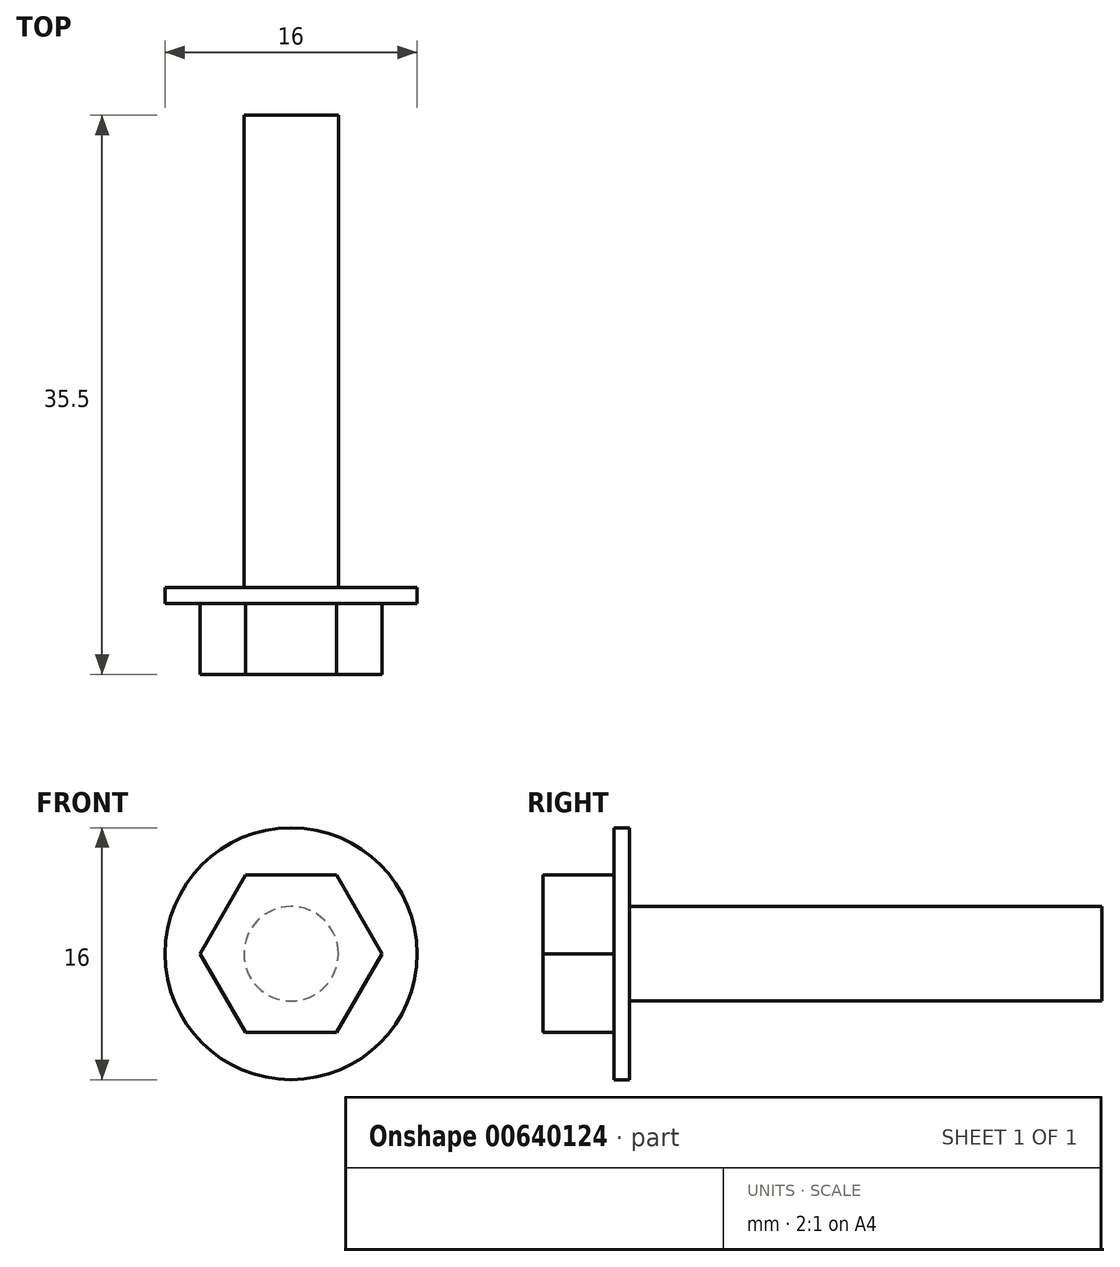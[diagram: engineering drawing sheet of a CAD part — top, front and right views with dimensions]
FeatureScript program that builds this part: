
annotation { "Feature Type Name" : "Feature", "Feature Type Description" : "" }
export const myFeature = defineFeature(function(context is Context, id is Id, definition is map)
    precondition{}
    {
        {
            var Q0;
            Q0=qCreatedBy(makeId("Front.planeOp"),FACE);
            var sketch = newSketch(context, id + "F0", { "sketchPlane" : qUnion([Q0])});
            skLineSegment(sketch, "E0", {"start": v(2.89, 0) * mm, "end": v(8.66, 0) * mm});
            skLineSegment(sketch, "E1", {"start": v(8.66, 0) * mm, "end": v(11.55, 5) * mm});
            skLineSegment(sketch, "E2", {"start": v(11.55, 5) * mm, "end": v(8.66, 10) * mm});
            skLineSegment(sketch, "E3", {"start": v(8.66, 10) * mm, "end": v(2.89, 10) * mm});
            skLineSegment(sketch, "E4", {"start": v(2.89, 10) * mm, "end": v(0, 5) * mm});
            skLineSegment(sketch, "E5", {"start": v(0, 5) * mm, "end": v(2.89, 0) * mm});
            skLineSegment(sketch, "E6", {"start": v(2.89, 10) * mm, "end": v(8.66, 0) * mm, "construction": true});
            skLineSegment(sketch, "E7", {"start": v(2.89, 0) * mm, "end": v(8.66, 10) * mm, "construction": true});
            skLineSegment(sketch, "E8", {"start": v(0, 5) * mm, "end": v(11.55, 5) * mm, "construction": true});
            skSolve(sketch);
        }
        {
            var Q0;
            Q0 = qSketchRegion(id + "F0", true);
            extrude(context, id + "F1", {"entities" : qUnion([Q0]), "depth" : 5.5 * mm, "offsetDistance" : 25 * mm});
        }
        {
            var Q0;
            Q0=makeQuery(id+"F1.opExtrude","CAP_FACE",FACE,{"disambiguationData":[OSD([sQuery(id+"F0.wireOp",EDGE,"E0"),sQuery(id+"F0.wireOp",EDGE,"E1"),sQuery(id+"F0.wireOp",EDGE,"E2"),sQuery(id+"F0.wireOp",EDGE,"E3"),sQuery(id+"F0.wireOp",EDGE,"E4"),sQuery(id+"F0.wireOp",EDGE,"E5")])],"isStart":true});
            var sketch = newSketch(context, id + "F2", { "sketchPlane" : qUnion([Q0])});
            skCircle(sketch, "E9", {"center": v(-5.77, 5) * mm, "radius": 8 * mm});
            skPoint(sketch, "E9.centerSnap0", {"position": v(-5.77, 10) * mm});
            skLineSegment(sketch, "E10", {"start": v(-5.77, 5) * mm, "end": v(0, 5) * mm, "construction": true});
            skLineSegment(sketch, "E11", {"start": v(-5.77, 5) * mm, "end": v(-8.66, 0) * mm, "construction": true});
            skSolve(sketch);
        }
        {
            var Q0;
            Q0=makeQuery(id+"F2.imprint","IMPRINT",FACE,{"disambiguationData":[TD([[makeQuery(id+"F2.imprint","IMPRINT",EDGE,{"derivedFrom":sQuery(id+"F2.wireOp",EDGE,"E9")}),1.0]])]});
            extrude(context, id + "F3", {"entities" : qUnion([Q0]), "operationType" : NewBodyOperationType.ADD, "oppositeDirection" : true, "depth" : 1 * mm, "offsetDistance" : 25 * mm});
        }
        {
            var Q0;
            {var subQ0=sQuery(id+"F0.wireOp",EDGE,"E5");var subQ1=sQuery(id+"F0.wireOp",EDGE,"E4");var subQ2=sQuery(id+"F0.wireOp",EDGE,"E3");var subQ3=sQuery(id+"F0.wireOp",EDGE,"E2");var subQ4=sQuery(id+"F0.wireOp",EDGE,"E1");var subQ5=sQuery(id+"F0.wireOp",EDGE,"E0");Q0=makeQuery(id+"F3.boolean.opBoolean","MERGE",FACE,{"derivedFrom":[makeQuery(id+"F1.opExtrude","CAP_FACE",FACE,{"disambiguationData":[OSD([subQ5,subQ4,subQ3,subQ2,subQ1,subQ0])],"isStart":true}),makeQuery(id+"F3.opExtrude","CAP_FACE",FACE,{"disambiguationData":[OSD([subQ5,subQ4,subQ3,subQ2,subQ1,subQ0,sQuery(id+"F2.wireOp",EDGE,"E9")])],"isStart":true})]});}
            var sketch = newSketch(context, id + "F4", { "sketchPlane" : qUnion([Q0])});
            skCircle(sketch, "E12", {"center": v(-5.77, 5) * mm, "radius": 3 * mm});
            skSolve(sketch);
        }
        {
            var Q0;
            Q0 = qSketchRegion(id + "F4", true);
            extrude(context, id + "F5", {"entities" : qUnion([Q0]), "operationType" : NewBodyOperationType.ADD, "depth" : 30 * mm, "offsetDistance" : 25 * mm});
        }
    });
